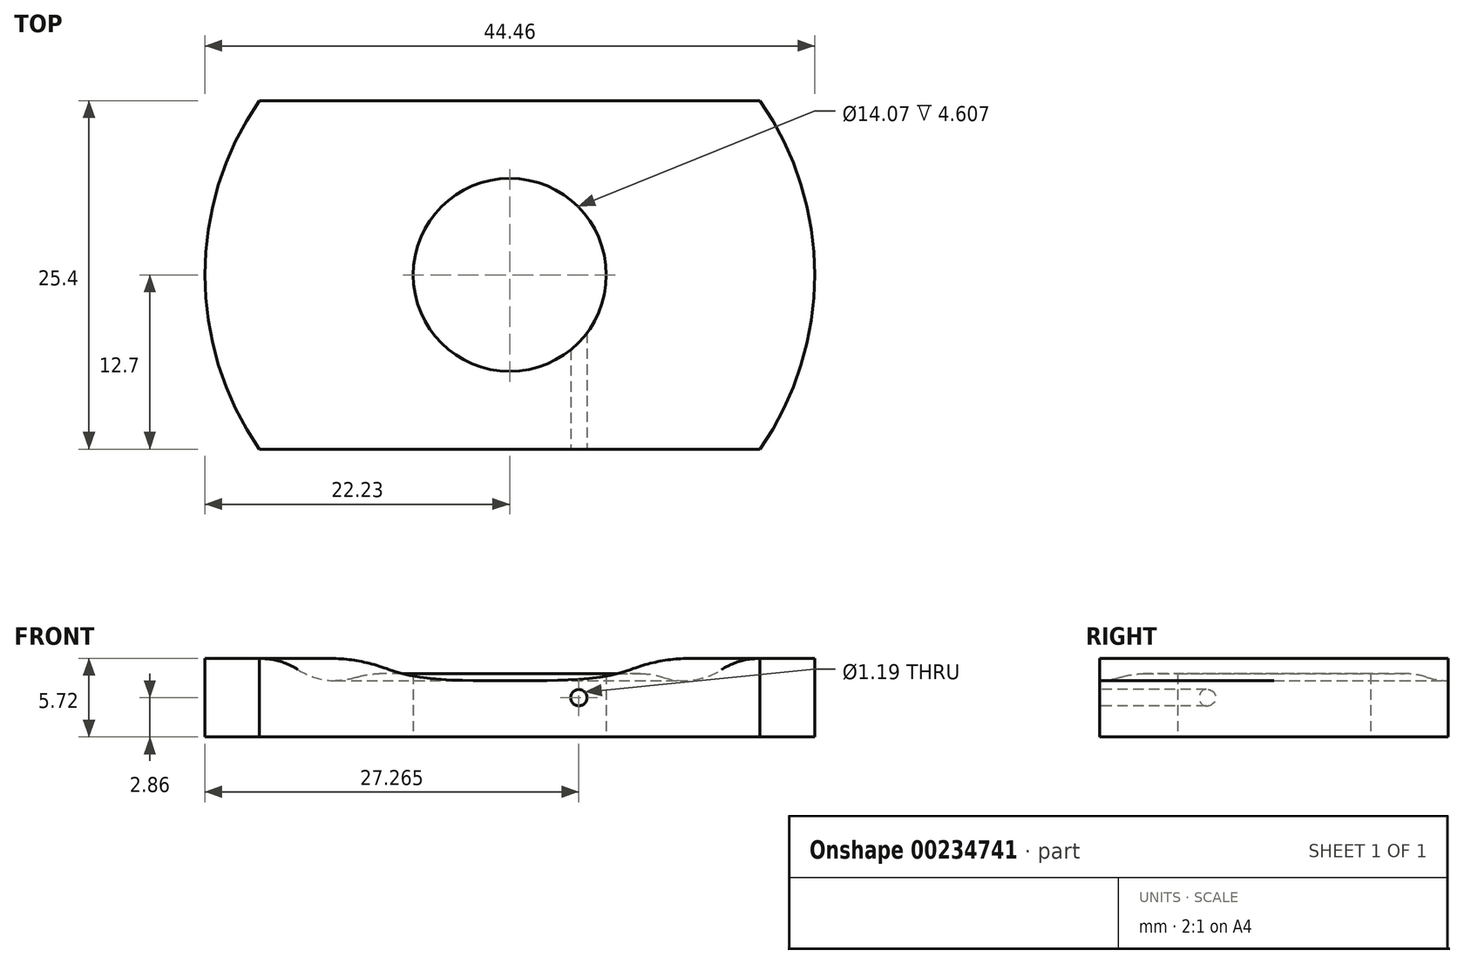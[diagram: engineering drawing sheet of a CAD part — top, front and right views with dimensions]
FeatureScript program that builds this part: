
annotation { "Feature Type Name" : "Feature", "Feature Type Description" : "" }
export const myFeature = defineFeature(function(context is Context, id is Id, definition is map)
    precondition{}
    {
        {
            var Q0;
            Q0=qCreatedBy(makeId("Top.planeOp"),FACE);
            var sketch = newSketch(context, id + "F0", { "sketchPlane" : qUnion([Q0])});
            skArc(sketch, "E0", {"start": v(-18.24, 12.7) * mm, "mid": v(-22.23, 0) * mm, "end": v(-18.24, -12.7) * mm});
            skLineSegment(sketch, "E1.bottom", {"start": v(18.24, 12.7) * mm, "end": v(-18.24, 12.7) * mm});
            skLineSegment(sketch, "E1.top", {"start": v(18.24, -12.7) * mm, "end": v(-18.24, -12.7) * mm});
            skLineSegment(sketch, "E1.left", {"start": v(18.24, 12.7) * mm, "end": v(18.24, -12.7) * mm, "construction": true});
            skLineSegment(sketch, "E1.right", {"start": v(-18.24, 12.7) * mm, "end": v(-18.24, -12.7) * mm, "construction": true});
            skArc(sketch, "E2.trimOffspring", {"start": v(18.24, -12.7) * mm, "mid": v(22.23, 0) * mm, "end": v(18.24, 12.7) * mm});
            skCircle(sketch, "E3", {"center": v(0, 0) * mm, "radius": 7.04 * mm});
            skSolve(sketch);
        }
        {
            var Q0;
            Q0 = qSketchRegion(id + "F0", true);
            extrude(context, id + "F1", {"entities" : qUnion([Q0]), "endBound" : BoundingType.SYMMETRIC, "depth" : 5.7 * mm});
        }
        {
            var Q0;
            Q0=qCreatedBy(makeId("Front.planeOp"),FACE);
            var sketch = newSketch(context, id + "F2", { "sketchPlane" : qUnion([Q0])});
            skCircle(sketch, "E4", {"center": v(12.7, 6.32) * mm, "radius": 5.08 * mm});
            skLineSegment(sketch, "E5", {"start": v(12.7, 6.32) * mm, "end": v(12.7, 2.86) * mm});
            skLineSegment(sketch, "E6", {"start": v(12.7, 2.86) * mm, "end": v(12.7, 1.24) * mm});
            skLineSegment(sketch, "E7", {"start": v(7.62, 6.3) * mm, "end": v(0, 6.3) * mm});
            skLineSegment(sketch, "E8", {"start": v(0, 6.3) * mm, "end": v(0, 1.75) * mm});
            skLineSegment(sketch, "E9", {"start": v(0, 1.75) * mm, "end": v(10.49, 1.75) * mm});
            skLineSegment(sketch, "E10", {"start": v(0, 0) * mm, "end": v(-5.27, 0) * mm, "construction": true});
            skSolve(sketch);
        }
        {
            var Q0;
            Q0 = qSketchRegion(id + "F2", true);
            var Q1;
            Q1=makeQuery(id+"F1.opExtrude","SWEPT_FACE",FACE,{"disambiguationData":[OSD([sQuery(id+"F0.wireOp",EDGE,"E3")])]});
            revolve(context, id + "F3", {"operationType" : NewBodyOperationType.REMOVE, "entities" : qUnion([Q0]), "axis" : qUnion([Q1]), "revolveType" : RevolveType.FULL, "oppositeDirection" : true});
        }
        {
            var Q0;
            Q0=makeQuery(id+"F3.boolean.opBoolean","INTERSECT",EDGE,{"disambiguationData":[OD(1.0)],"derivedFrom":[makeQuery(id+"F1.opExtrude","CAP_FACE",FACE,{"disambiguationData":[OSD([sQuery(id+"F0.wireOp",EDGE,"E0"),sQuery(id+"F0.wireOp",EDGE,"E1.bottom"),sQuery(id+"F0.wireOp",EDGE,"E1.top"),sQuery(id+"F0.wireOp",EDGE,"E2.trimOffspring"),sQuery(id+"F0.wireOp",EDGE,"E3")])],"isStart":false}),makeQuery(id+"F3.opRevolve","SWEPT_FACE",FACE,{"disambiguationData":[OSD([sQuery(id+"F2.wireOp",EDGE,"E4")])]})]});
            var Q1;
            Q1=makeQuery(id+"F3.boolean.opBoolean","INTERSECT",EDGE,{"disambiguationData":[OD(0.0)],"derivedFrom":[makeQuery(id+"F1.opExtrude","CAP_FACE",FACE,{"disambiguationData":[OSD([sQuery(id+"F0.wireOp",EDGE,"E0"),sQuery(id+"F0.wireOp",EDGE,"E1.bottom"),sQuery(id+"F0.wireOp",EDGE,"E1.top"),sQuery(id+"F0.wireOp",EDGE,"E2.trimOffspring"),sQuery(id+"F0.wireOp",EDGE,"E3")])],"isStart":false}),makeQuery(id+"F3.opRevolve","SWEPT_FACE",FACE,{"disambiguationData":[OSD([sQuery(id+"F2.wireOp",EDGE,"E4")])]})]});
            var Q2;
            Q2=makeQuery(id+"F3.boolean.opBoolean","COPY",EDGE,{"derivedFrom":makeQuery(id+"F3.opRevolve","SWEPT_EDGE",EDGE,{"disambiguationData":[OSD([sQuery(id+"F2.wireOp",EDGE,"E4"),sQuery(id+"F2.wireOp",EDGE,"E9")])]})});
            var Q3;
            Q3=makeQuery(id+"FBVG78wqvWEtJCH_1.1.F3.boolean.opBoolean","INTERSECT",EDGE,{"disambiguationData":[OD(1.0)],"derivedFrom":[makeQuery(id+"F1.opExtrude","CAP_FACE",FACE,{"disambiguationData":[OSD([sQuery(id+"F0.wireOp",EDGE,"E0"),sQuery(id+"F0.wireOp",EDGE,"E1.bottom"),sQuery(id+"F0.wireOp",EDGE,"E1.top"),sQuery(id+"F0.wireOp",EDGE,"E2.trimOffspring"),sQuery(id+"F0.wireOp",EDGE,"E3")])],"isStart":true}),makeQuery(id+"FBVG78wqvWEtJCH_1.1.F3.opRevolve","SWEPT_FACE",FACE,{"disambiguationData":[OSD([sQuery(id+"F2.wireOp",EDGE,"E4")])]})]});
            var Q4;
            Q4=makeQuery(id+"FBVG78wqvWEtJCH_1.1.F3.boolean.opBoolean","COPY",EDGE,{"derivedFrom":makeQuery(id+"FBVG78wqvWEtJCH_1.1.F3.opRevolve","SWEPT_EDGE",EDGE,{"disambiguationData":[OSD([sQuery(id+"F2.wireOp",EDGE,"E4"),sQuery(id+"F2.wireOp",EDGE,"E9")])]})});
            var Q5;
            Q5=makeQuery(id+"FBVG78wqvWEtJCH_1.1.F3.boolean.opBoolean","INTERSECT",EDGE,{"disambiguationData":[OD(0.0)],"derivedFrom":[makeQuery(id+"F1.opExtrude","CAP_FACE",FACE,{"disambiguationData":[OSD([sQuery(id+"F0.wireOp",EDGE,"E0"),sQuery(id+"F0.wireOp",EDGE,"E1.bottom"),sQuery(id+"F0.wireOp",EDGE,"E1.top"),sQuery(id+"F0.wireOp",EDGE,"E2.trimOffspring"),sQuery(id+"F0.wireOp",EDGE,"E3")])],"isStart":true}),makeQuery(id+"FBVG78wqvWEtJCH_1.1.F3.opRevolve","SWEPT_FACE",FACE,{"disambiguationData":[OSD([sQuery(id+"F2.wireOp",EDGE,"E4")])]})]});
            fillet(context, id + "F4", {"entities" : qUnion([Q0, Q1, Q2, Q3, Q4, Q5]), "radius" : 5.08 * mm, "tangentPropagation" : true, "allowEdgeOverflow" : false});
        }
        {
            var Q0;
            Q0=makeQuery(id+"F1.opExtrude","SWEPT_FACE",FACE,{"disambiguationData":[OSD([sQuery(id+"F0.wireOp",EDGE,"E1.top")])]});
            var sketch = newSketch(context, id + "F5", { "sketchPlane" : qUnion([Q0])});
            skLineSegment(sketch, "E11", {"start": v(7.04, 1.75) * mm, "end": v(7.04, -1.75) * mm, "construction": true});
            skLineSegment(sketch, "E12", {"start": v(7.04, 0) * mm, "end": v(5.04, 0) * mm, "construction": true});
            skPoint(sketch, "E13", {"position": v(5.04, 0) * mm});
            skLineSegment(sketch, "E14.0", {"start": v(-7.04, 1.75) * mm, "end": v(7.04, 1.75) * mm, "construction": true});
            skSolve(sketch);
        }
        {
            var Q0;
            Q0=sQuery(id+"F5.wireOp",VERTEX,"E13");
            var Q1;
            Q1=makeQuery(id+"F1.opExtrude","SWEPT_BODY",BODY,{"disambiguationData":[OSD([sQuery(id+"F0.wireOp",EDGE,"E0"),sQuery(id+"F0.wireOp",EDGE,"E1.bottom"),sQuery(id+"F0.wireOp",EDGE,"E1.top"),sQuery(id+"F0.wireOp",EDGE,"E2.trimOffspring"),sQuery(id+"F0.wireOp",EDGE,"E3")])]});
            hole(context, id + "F6", {"style" : HoleStyle.SIMPLE, "endStyle" : HoleEndStyle.BLIND, "standardTappedOrClearance" : lookupTablePath({ "standard" : "ANSI", "engagement" : "75%", "pitch" : "80 tpi", "size" : "#0", "type" : "Tapped" }), "standardBlindInLast" : lookupTablePath({ "standard" : "ANSI", "engagement" : "75%", "pitch" : "80 tpi", "size" : "#0", "type" : "Tapped" }), "holeDiameter" : 1.2 * mm, "holeDepth" : 12.7 * mm, "startFromSketch" : true, "locations" : qUnion([Q0]), "scope" : qUnion([Q1]), "majorDiameter" : 1.52 * mm});
        }
    });
